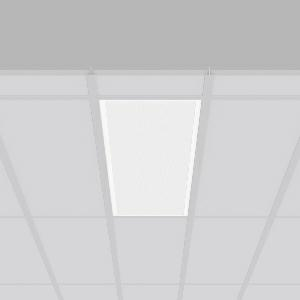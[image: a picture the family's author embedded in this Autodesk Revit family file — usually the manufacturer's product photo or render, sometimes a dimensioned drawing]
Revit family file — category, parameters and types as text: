
# Revit family: sidelite_eco_312366_002_1_76_42e7
name_source: partatom
category: Lighting Fixtures
units: mm (PartAtom-declared; Revit-internal decimal feet)

## family parameters
Cut with Voids When Loaded = No
Host = Face
Light Source = No
Part Type = Normal
Room Calculation Point = No
Round Connector Dimension = Use Diameter
Shared = No

## types (1)
- MultiLumen 1 (1 x LED Modul 840, 3500 lm, 4000)
    Apparent Load = 29 VA
    CIE Flux Codes = 63 88 97 100 100
    Color Rendering = 80
    Color Temperature = 4000
    Default Elevation = 1800 mm
    Description = Series: SIDELITE ECO
Highly economical recessed luminaire with progressive LED technology. Frame made of aluminium, powder-coated. Diffuser plastic microprismatic. Lightguide and diffuser made of non-yellowing plastic (PMMA). Lateral light emission (RZB SIDELITE technology) for homogeneous light distribution. External driver. External driver with simple plug-in locking system and extended converter connecting cable to luminaire (1.90 m). MultiLumen: 4 steps adjustable luminous flux. Factory setting is the lowest offered step. Luminaire can be used with accessories (to be ordered separately) for recessed, surface mounting or as pendant luminaire. Perfect for office areas (RUG < 19) and environments with computer screens in accordance with EN 12464-1. Qualified for use in the food and drink industry. 
Colour: white
Length: 1195 mm
Width: 295 mm
Cut-out length: 1180 mm
Cut-out width: 280 mm
Recess height: 160 mm
Luminaire: recess height: 38 mm
Lamp: LED
Socket: without socket
Colour temperature: 4000K
Colour rendering index (CRI): 80
System power: 29 W
Rated luminous flux: 3500 lm
Luminous efficiency: 121 lm/W
System power 2: 33 W
Rated luminous flux 2: 3850 lm
Luminous efficiency 2: 117 lm/W
System power 3: 35 W
Rated luminous flux 3: 4050 lm
Luminous efficiency 3: 116 lm/W
System power 4: 38 W
Rated luminous flux 4: 4400 lm
Luminous efficiency 4: 116 lm/W
Control gear: Converter, dimmable, DALI
Protection class: II
Type of protection: IP 40
    Height = 0 mm  [stored 0 ft]
    Lamp = 1 x LED Modul 840
    Lamp Light Flux = 3500 lm
    Lamp count = 1
    Length = 1195 mm
    Lifetime = 50000 h
    Luminous efficacy = 121 lm/W
    Manufacturer = RZB
    ModVariant = No
    Model = 312366.002.1.76
    Mounting Place = Ceiling
    Mounting Type = Recessed
    Number of Poles = 1
    OnlyDefault = Yes
    Power Factor = 1
    Product Name = SIDELITE ECO
    Product group = Recessed modular luminaires
    ProductGroupID = 406
    Protection Class = Protection class II
    Protection Degree = IP 20
    RLX_Detail_Level = 1
    RLX_Emergency_Light_Flux = 0 lm
    RLX_Emergency_Type = 0
    RLX_Emergency_Type_DB = No
    RlxData = <blob elided: 36089 chars, md5=91c217b1>
    Socket = socket
    Standby Power = 0 W
    System Light Flux = 3500 lm
    System Power = 29 W
    Type Comments = MultiLumen 1
    Type Image = 312366.002.jpg
    URL = http://relux.com
    VarID = multilumen_1
    Voltage = 230 V
    Voltage Range = 220-240 V
    Weight = 0.00 kg
    Width = 295 mm

note: [stored X ft] marks values corroborated as IEEE doubles in the binary element streams (Revit-internal decimal feet)

## geometry (parser evidence)
native form markers: Blend x4, Sweep x10
no freeform markers — native parametric forms only
